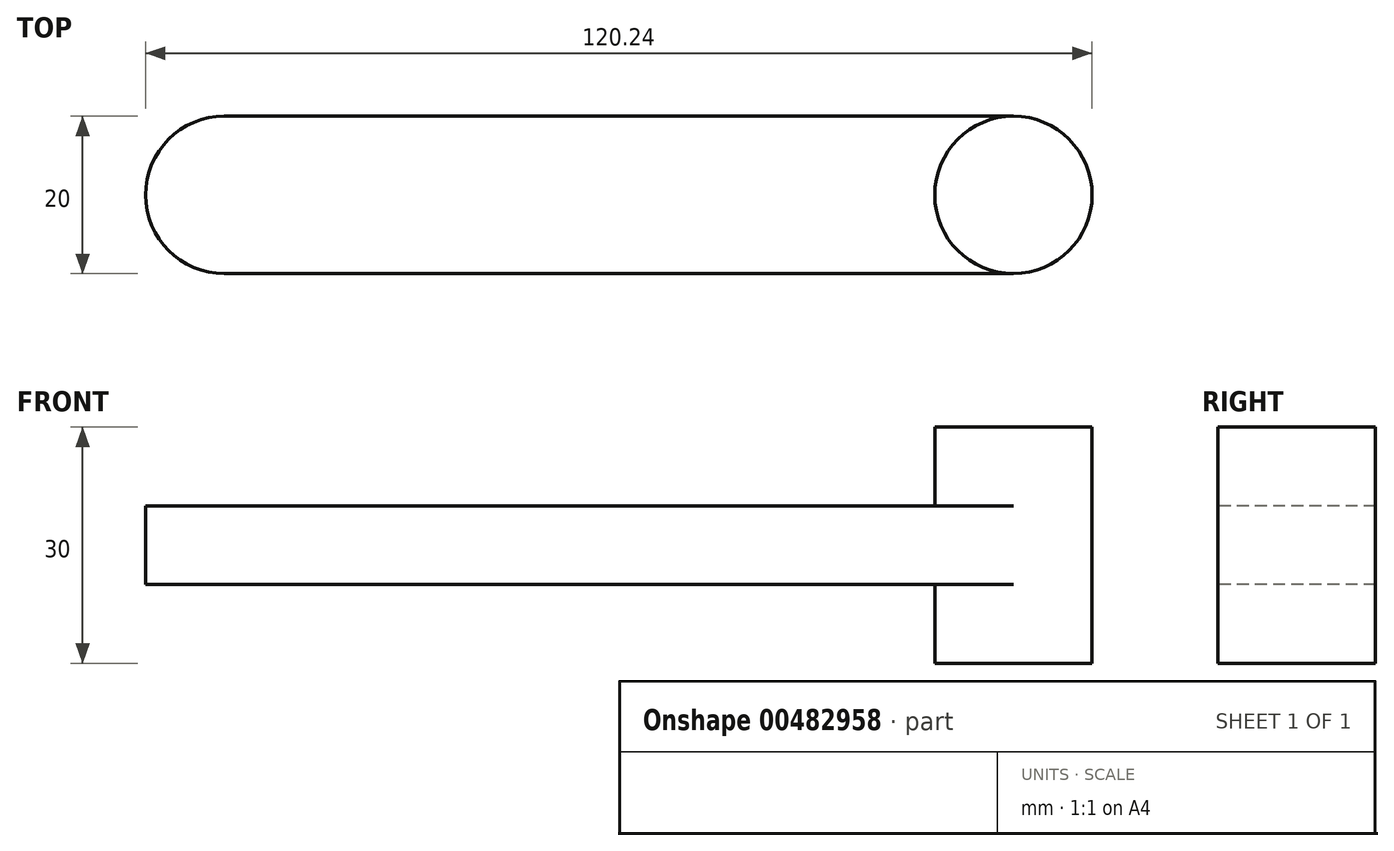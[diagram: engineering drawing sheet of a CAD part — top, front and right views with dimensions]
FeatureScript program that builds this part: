
annotation { "Feature Type Name" : "Feature", "Feature Type Description" : "" }
export const myFeature = defineFeature(function(context is Context, id is Id, definition is map)
    precondition{}
    {
        {
            var Q0;
            Q0=qCreatedBy(makeId("Top.planeOp"),FACE);
            var sketch = newSketch(context, id + "F0", { "sketchPlane" : qUnion([Q0])});
            skArc(sketch, "E0.0.startCap", {"start": v(-100.24, -10) * mm, "mid": v(-110.24, 0) * mm, "end": v(-100.24, 10) * mm});
            skArc(sketch, "E0.0.endCap", {"start": v(99.76, 10) * mm, "mid": v(109.76, 0) * mm, "end": v(99.76, -10) * mm});
            skLineSegment(sketch, "E0.0.left", {"start": v(-100.24, 10) * mm, "end": v(99.76, 10) * mm});
            skLineSegment(sketch, "E0.0.right", {"start": v(-100.24, -10) * mm, "end": v(99.76, -10) * mm});
            skLineSegment(sketch, "E1.0", {"start": v(-100.24, 32) * mm, "end": v(99.76, 32) * mm});
            skArc(sketch, "E1.1", {"start": v(-100.24, -32) * mm, "mid": v(-132.24, 0) * mm, "end": v(-100.24, 32) * mm});
            skLineSegment(sketch, "E1.2", {"start": v(-100.24, -32) * mm, "end": v(99.76, -32) * mm});
            skArc(sketch, "E1.3", {"start": v(99.76, 32) * mm, "mid": v(131.76, 0) * mm, "end": v(99.76, -32) * mm});
            skCircle(sketch, "E2", {"center": v(0, 0) * mm, "radius": 10 * mm});
            skSolve(sketch);
        }
        {
            var Q0;
            {var subQ4=sQuery(id+"F0.wireOp",EDGE,"E0.0.startCap");Q0=makeQuery(id+"F0.imprint","IMPRINT",FACE,{"disambiguationData":[TD([[makeQuery(id+"F0.imprint","IMPRINT",EDGE,{"derivedFrom":subQ4}),1.0]])]});}
            extrude(context, id + "F1", {"entities" : qUnion([Q0]), "endBound" : BoundingType.SYMMETRIC, "depth" : 10 * mm});
        }
        {
            var Q0;
            {var subQ0=sQuery(id+"F0.wireOp",EDGE,"E2");var subQ1=makeQuery(id+"F0.imprint","INTERSECT",VERTEX,{"derivedFrom":[sQuery(id+"F0.wireOp",EDGE,"E0.0.left"),subQ0]});Q0=makeQuery(id+"F0.imprint","IMPRINT",FACE,{"disambiguationData":[TD([[makeQuery(id+"F0.imprint","IMPRINT",EDGE,{"disambiguationData":[TD([[subQ1,-1.0]])],"derivedFrom":subQ0}),1.0]])]});}
            extrude(context, id + "F2", {"entities" : qUnion([Q0]), "operationType" : NewBodyOperationType.ADD, "endBound" : BoundingType.SYMMETRIC, "depth" : 30 * mm});
        }
    });
